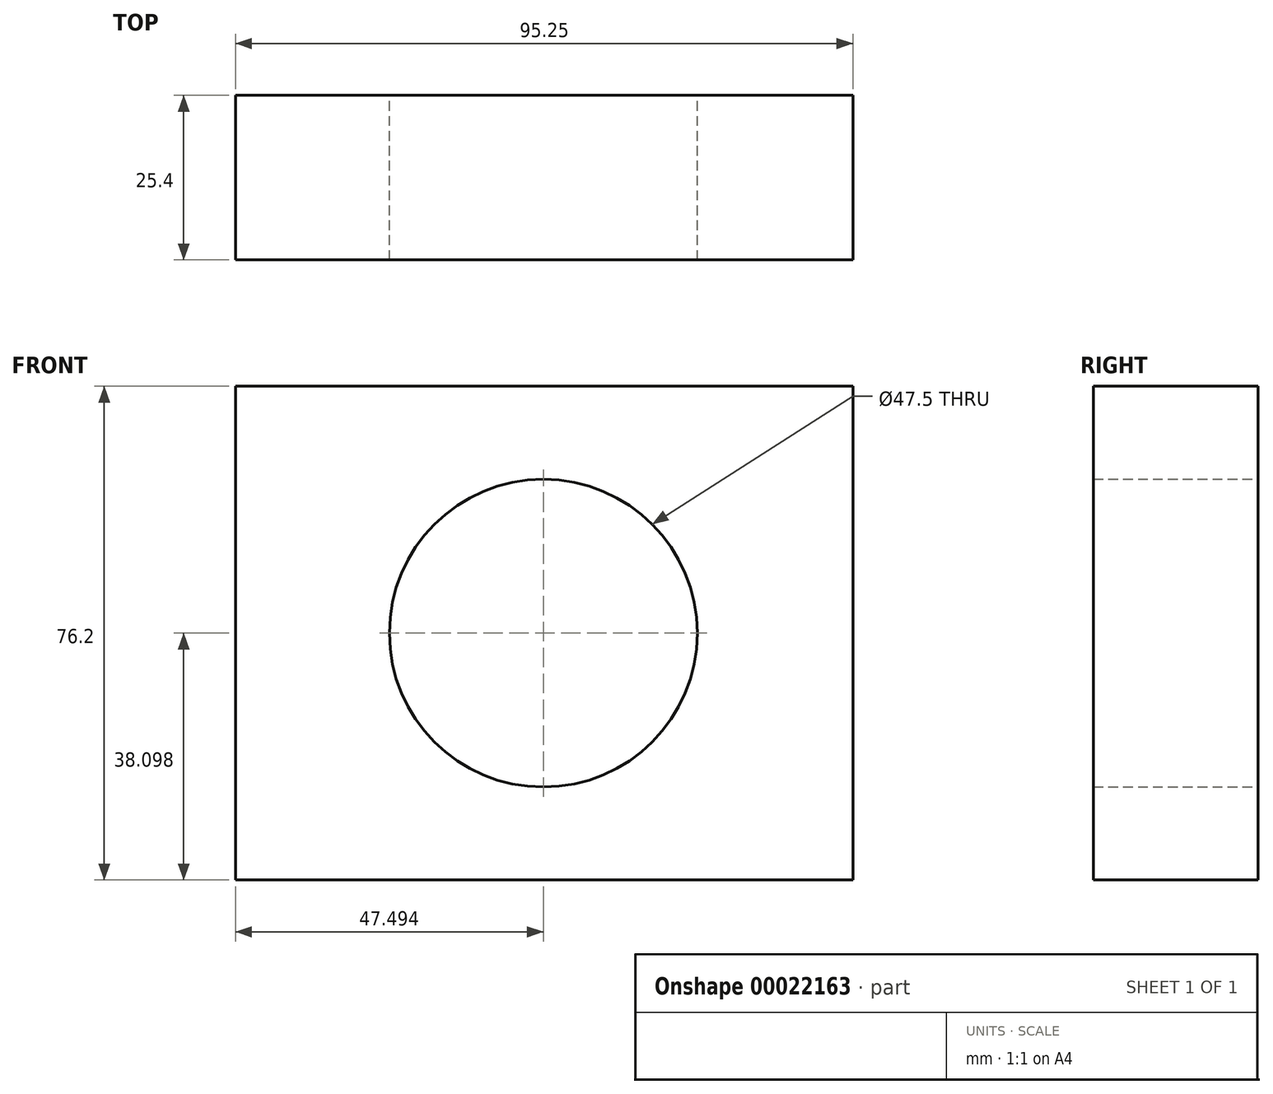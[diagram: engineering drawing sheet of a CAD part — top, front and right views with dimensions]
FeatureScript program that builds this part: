
annotation { "Feature Type Name" : "Feature", "Feature Type Description" : "" }
export const myFeature = defineFeature(function(context is Context, id is Id, definition is map)
    precondition{}
    {
        {
            var Q0;
            Q0=qCreatedBy(makeId("Front.planeOp"),FACE);
            var sketch = newSketch(context, id + "F0", { "sketchPlane" : qUnion([Q0])});
            skLineSegment(sketch, "E0.bottom", {"start": v(-36.9, 28.45) * mm, "end": v(58.36, 28.45) * mm});
            skLineSegment(sketch, "E0.top", {"start": v(-36.9, -47.75) * mm, "end": v(58.36, -47.75) * mm});
            skLineSegment(sketch, "E0.left", {"start": v(-36.9, 28.45) * mm, "end": v(-36.9, -47.75) * mm});
            skLineSegment(sketch, "E0.right", {"start": v(58.36, 28.45) * mm, "end": v(58.36, -47.75) * mm});
            skLineSegment(sketch, "E1.1", {"start": v(10.6, -19.3) * mm, "end": v(10.86, -19.3) * mm});
            skLineSegment(sketch, "E1.3", {"start": v(10.6, 0) * mm, "end": v(10.86, 0) * mm});
            skLineSegment(sketch, "E2.0", {"start": v(10.6, 28.45) * mm, "end": v(10.6, -47.75) * mm, "construction": true});
            skCircle(sketch, "E3", {"center": v(10.6, -9.65) * mm, "radius": 23.75 * mm});
            skSolve(sketch);
        }
        {
            var Q0;
            Q0 = qSketchRegion(id + "F0", true);
            extrude(context, id + "F1", {"entities" : qUnion([Q0]), "depth" : 25.4 * mm});
        }
    });
